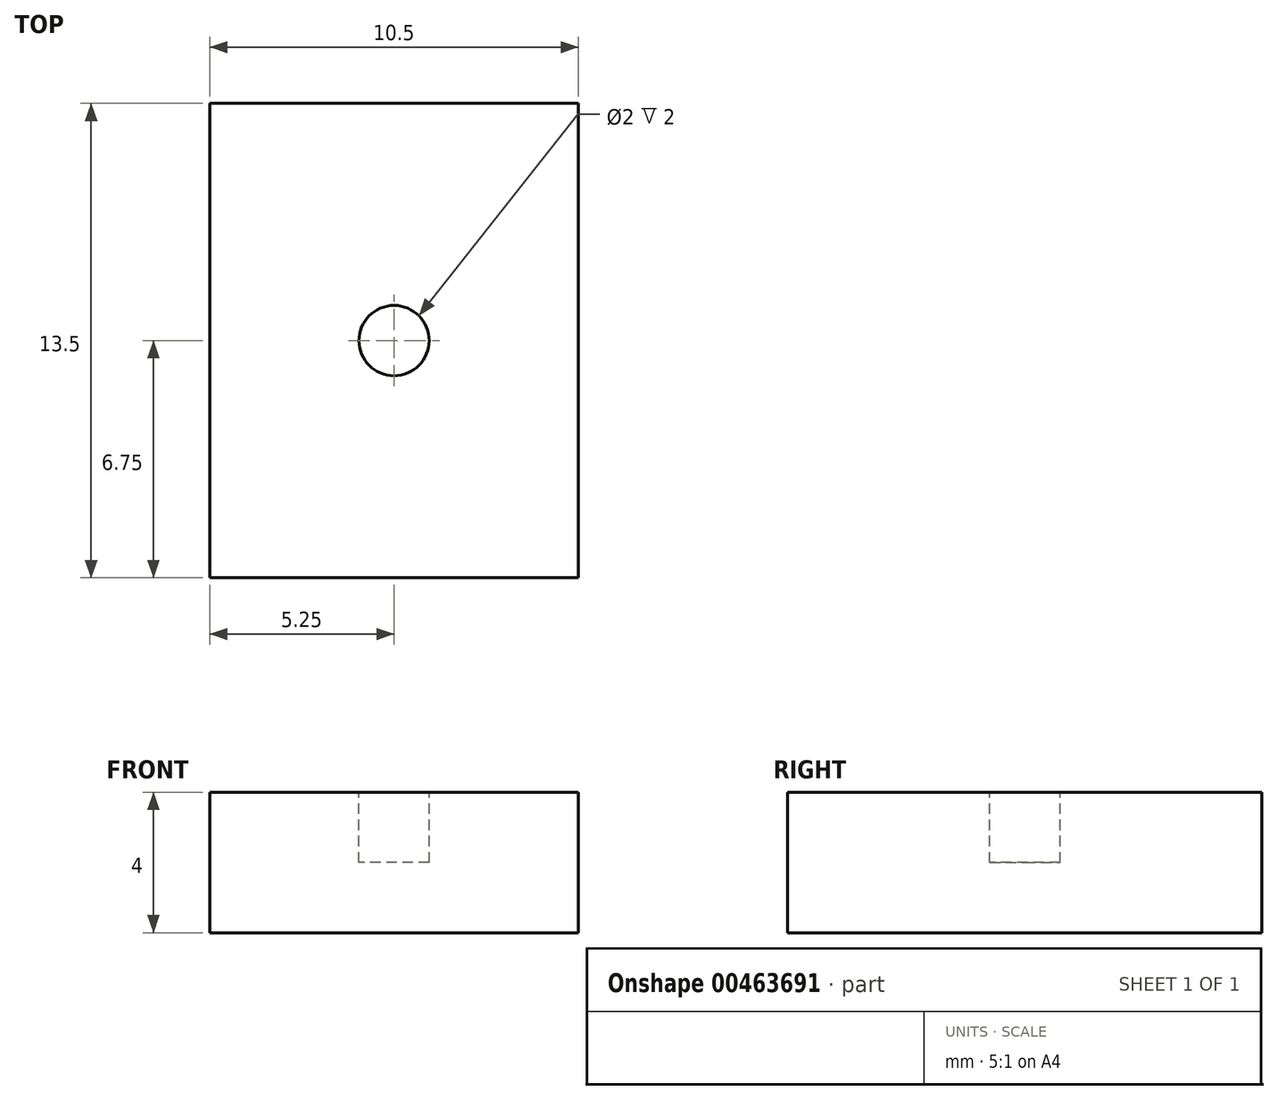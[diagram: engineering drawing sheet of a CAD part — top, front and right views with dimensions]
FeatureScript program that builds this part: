
annotation { "Feature Type Name" : "Feature", "Feature Type Description" : "" }
export const myFeature = defineFeature(function(context is Context, id is Id, definition is map)
    precondition{}
    {
        {
            var Q0;
            Q0=qCreatedBy(makeId("Top.planeOp"),FACE);
            var sketch = newSketch(context, id + "F0", { "sketchPlane" : qUnion([Q0])});
            skLineSegment(sketch, "E0.bottom", {"start": v(-5.25, 6.75) * mm, "end": v(5.25, 6.75) * mm});
            skLineSegment(sketch, "E0.top", {"start": v(-5.25, -6.75) * mm, "end": v(5.25, -6.75) * mm});
            skLineSegment(sketch, "E0.left", {"start": v(-5.25, 6.75) * mm, "end": v(-5.25, -6.75) * mm});
            skLineSegment(sketch, "E0.right", {"start": v(5.25, 6.75) * mm, "end": v(5.25, -6.75) * mm});
            skPoint(sketch, "E0.middle", {"position": v(0, 0) * mm});
            skSolve(sketch);
        }
        {
            var Q0;
            Q0=qSketchRegion(id+"F0",true);
            extrude(context, id + "F1", {"entities" : qUnion([Q0]), "depth" : 4 * mm});
        }
        {
            var Q0;
            Q0=makeQuery(id+"F1.opExtrude","CAP_FACE",FACE,{"disambiguationData":[OSD([sQuery(id+"F0.wireOp",EDGE,"E0.bottom"),sQuery(id+"F0.wireOp",EDGE,"E0.top"),sQuery(id+"F0.wireOp",EDGE,"E0.left"),sQuery(id+"F0.wireOp",EDGE,"E0.right")])],"isStart":false});
            var sketch = newSketch(context, id + "F2", { "sketchPlane" : qUnion([Q0])});
            skCircle(sketch, "E1", {"center": v(0, 0) * mm, "radius": 1 * mm});
            skSolve(sketch);
        }
        {
            var Q0;
            Q0 = qSketchRegion(id + "F2", true);
            extrude(context, id + "F3", {"entities" : qUnion([Q0]), "operationType" : NewBodyOperationType.REMOVE, "oppositeDirection" : true, "depth" : 2 * mm});
        }
    });
